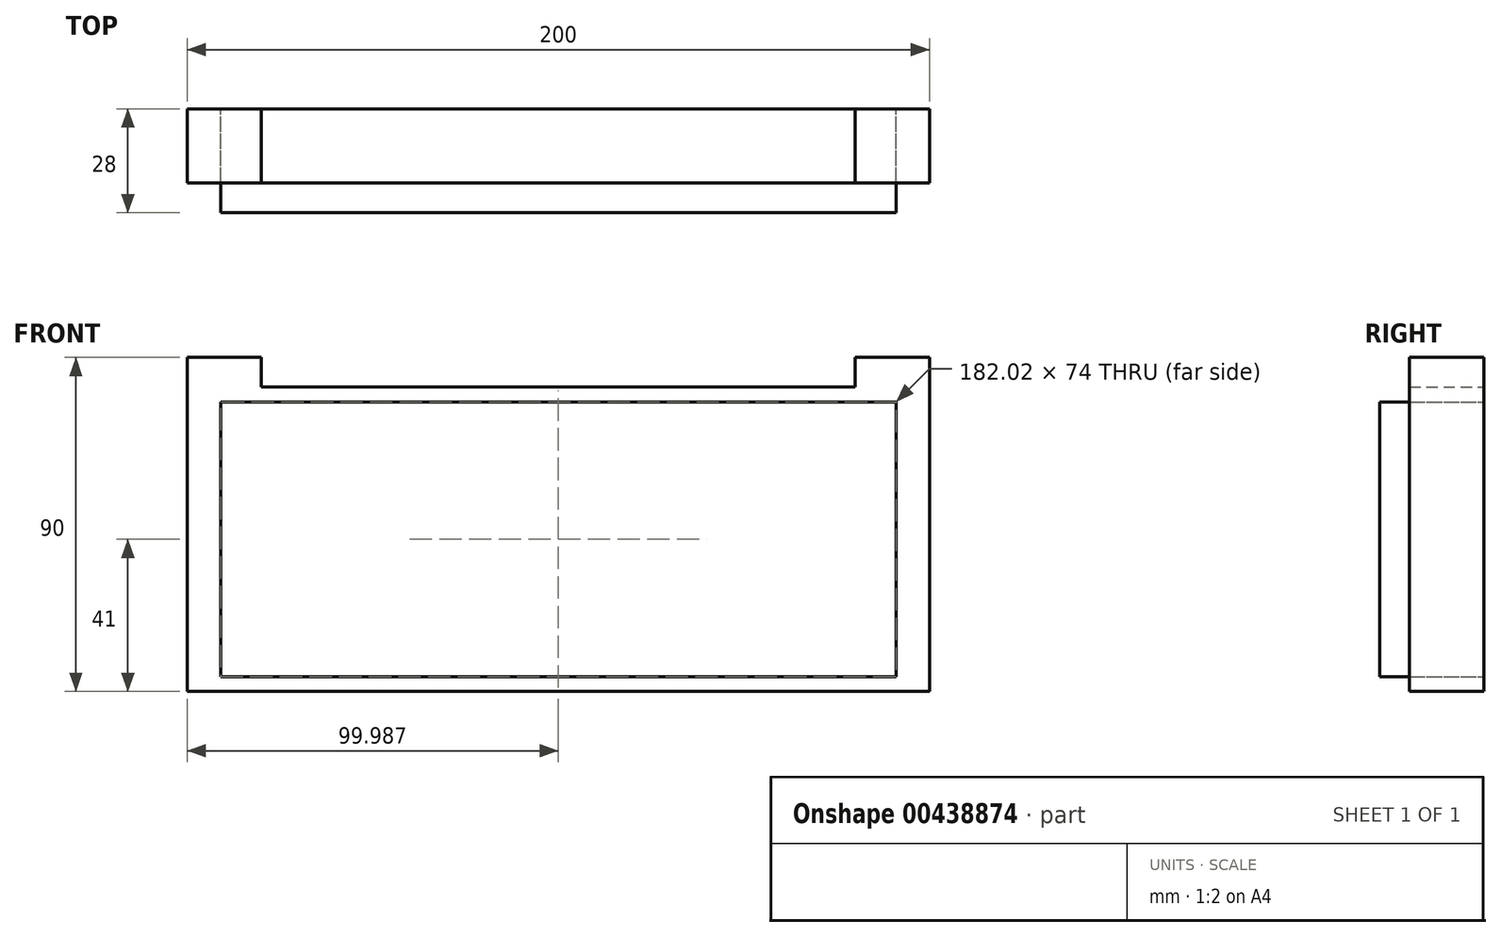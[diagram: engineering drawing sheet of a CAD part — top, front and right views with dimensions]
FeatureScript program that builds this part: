
annotation { "Feature Type Name" : "Feature", "Feature Type Description" : "" }
export const myFeature = defineFeature(function(context is Context, id is Id, definition is map)
    precondition{}
    {
        {
            var Q0;
            Q0=qCreatedBy(makeId("Front.planeOp"),FACE);
            var sketch = newSketch(context, id + "F0", { "sketchPlane" : qUnion([Q0])});
            skLineSegment(sketch, "E0.bottom", {"start": v(-98.85, 8) * mm, "end": v(101.15, 8) * mm});
            skLineSegment(sketch, "E0.top", {"start": v(-98.85, -82) * mm, "end": v(101.15, -82) * mm});
            skLineSegment(sketch, "E0.left", {"start": v(-98.85, 8) * mm, "end": v(-98.85, -82) * mm});
            skLineSegment(sketch, "E0.right", {"start": v(101.15, 8) * mm, "end": v(101.15, -82) * mm});
            skLineSegment(sketch, "E1.bottom", {"start": v(-78.85, 8) * mm, "end": v(81.15, 8) * mm});
            skLineSegment(sketch, "E1.top", {"start": v(-78.85, 0) * mm, "end": v(81.15, 0) * mm});
            skLineSegment(sketch, "E1.left", {"start": v(-78.85, 8) * mm, "end": v(-78.85, 0) * mm});
            skLineSegment(sketch, "E1.right", {"start": v(81.15, 8) * mm, "end": v(81.15, 0) * mm});
            skLineSegment(sketch, "E2.bottom", {"start": v(-89.87, -4) * mm, "end": v(92.15, -4) * mm});
            skLineSegment(sketch, "E2.top", {"start": v(-89.87, -78) * mm, "end": v(92.15, -78) * mm});
            skLineSegment(sketch, "E2.left", {"start": v(-89.87, -4) * mm, "end": v(-89.87, -78) * mm});
            skLineSegment(sketch, "E2.right", {"start": v(92.15, -4) * mm, "end": v(92.15, -78) * mm});
            skSolve(sketch);
        }
        {
            var Q0;
            Q0=makeQuery(id+"F0.imprint","IMPRINT",FACE,{"disambiguationData":[TD([[makeQuery(id+"F0.imprint","IMPRINT",EDGE,{"derivedFrom":sQuery(id+"F0.wireOp",EDGE,"E2.bottom")}),-1.0]])]});
            var Q1;
            Q1=makeQuery(id+"F0.imprint","IMPRINT",FACE,{"disambiguationData":[TD([[makeQuery(id+"F0.imprint","IMPRINT",EDGE,{"derivedFrom":sQuery(id+"F0.wireOp",EDGE,"E1.bottom")}),-1.0]])]});
            extrude(context, id + "F1", {"entities" : qUnion([Q0, Q1]), "depth" : 28 * mm});
        }
        {
            var Q0;
            Q0=makeQuery(id+"F0.imprint","IMPRINT",FACE,{"disambiguationData":[TD([[makeQuery(id+"F0.imprint","IMPRINT",EDGE,{"derivedFrom":sQuery(id+"F0.wireOp",EDGE,"E0.top")}),1.0]])]});
            extrude(context, id + "F2", {"entities" : qUnion([Q0]), "depth" : 20 * mm});
        }
    });
